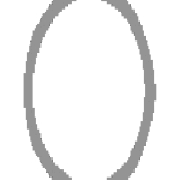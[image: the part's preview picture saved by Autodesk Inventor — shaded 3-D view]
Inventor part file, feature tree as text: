
AUTODESK INVENTOR PART (.ipt)
format: ipt  version: 2021 (Build 250183000, 183)  size: 112,640 bytes
history: native  units: in
note: dims shown in document units (in); Inventor stores cm internally (conversion verified against a paired STEP export)
features: other x4, sketch x3, plane x1
ambient origin geometry x8: Origin, YZ Plane, XZ Plane, XY Plane, X Axis, Y Axis, Z Axis, Center Point
bodies: Solid1 (feature_tree), Body (feature_tree)
feature tree (8):
  other  "Driven Length"
  other  "Frame Generator"
  other  "Start Plane"
  other  "End Plane"
  sketch  "Sketch"  dims[d2=20.5in d4=-0.0in d5=20.5in d6=0.12in d7=0.0in d8=90.0deg d9=20.5in]
  sketch  "Sketch2"  dims[d0=1.0in]
  plane  "Work Plane3"
  sketch  "Sketch3"  dims[d1=0.065in]
